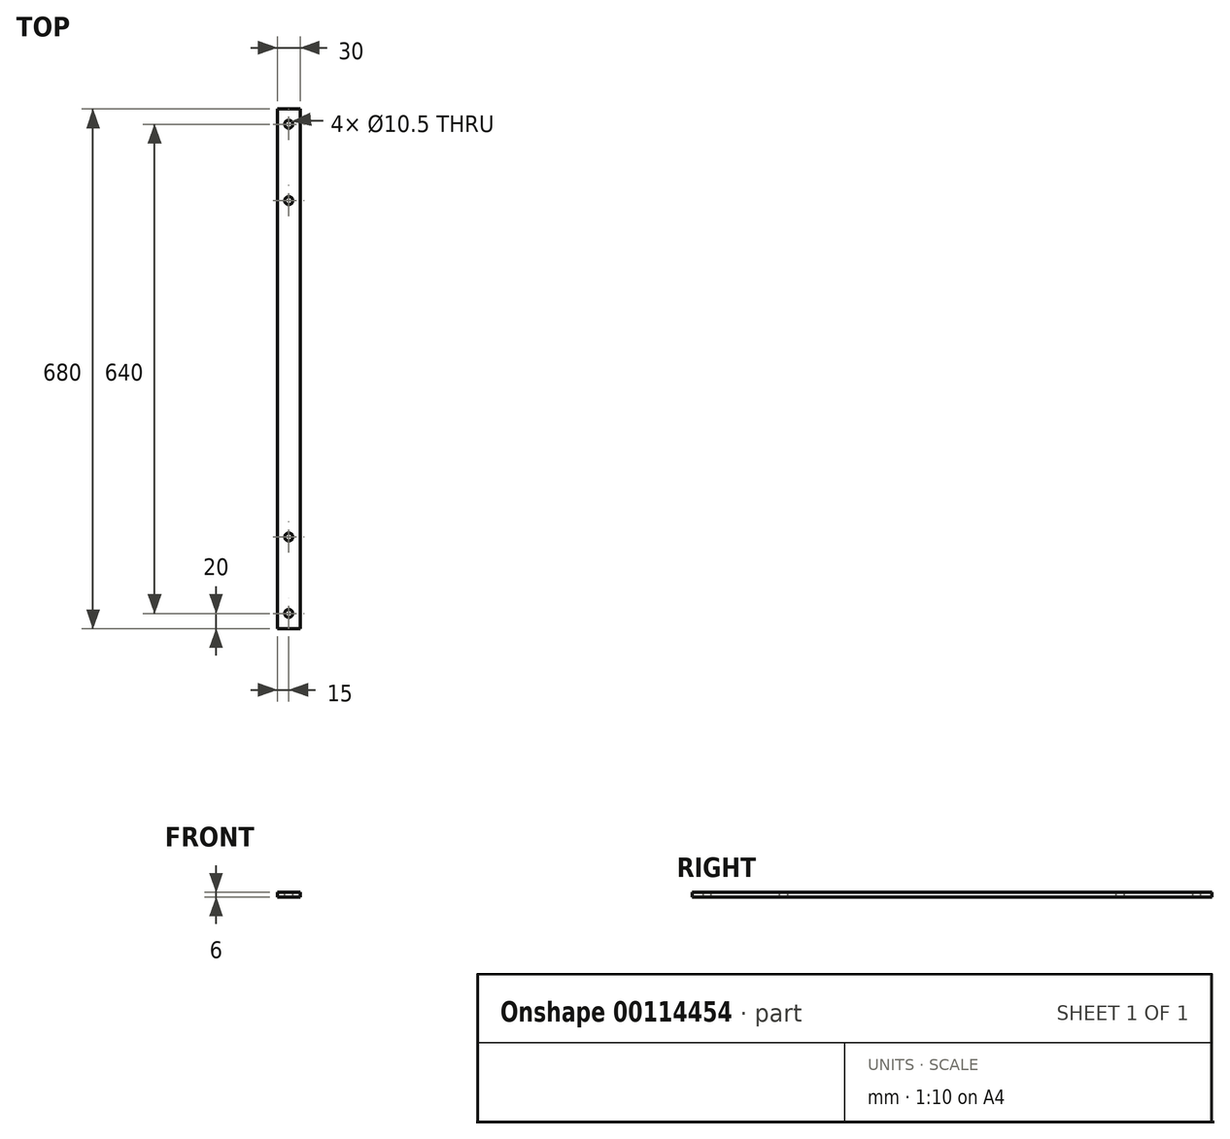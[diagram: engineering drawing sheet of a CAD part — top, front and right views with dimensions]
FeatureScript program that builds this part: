
annotation { "Feature Type Name" : "Feature", "Feature Type Description" : "" }
export const myFeature = defineFeature(function(context is Context, id is Id, definition is map)
    precondition{}
    {
        {
            var Q0;
            Q0=qCreatedBy(makeId("Top.planeOp"),FACE);
            var sketch = newSketch(context, id + "F0", { "sketchPlane" : qUnion([Q0])});
            skLineSegment(sketch, "E0.bottom", {"start": v(15, -340) * mm, "end": v(-15, -340) * mm});
            skLineSegment(sketch, "E0.top", {"start": v(15, 340) * mm, "end": v(-15, 340) * mm});
            skLineSegment(sketch, "E0.left", {"start": v(15, -340) * mm, "end": v(15, 340) * mm});
            skLineSegment(sketch, "E0.right", {"start": v(-15, -340) * mm, "end": v(-15, 340) * mm});
            skPoint(sketch, "E0.middle", {"position": v(0, 0) * mm});
            skSolve(sketch);
        }
        {
            var Q0;
            Q0=makeQuery(id+"F0.imprint","IMPRINT",FACE,{"disambiguationData":[TD([[makeQuery(id+"F0.imprint","IMPRINT",EDGE,{"derivedFrom":sQuery(id+"F0.wireOp",EDGE,"E0.bottom")}),-1.0]])]});
            extrude(context, id + "F1", {"entities" : qUnion([Q0]), "depth" : 6 * mm});
        }
        {
            var Q0;
            Q0=makeQuery(id+"F1.opExtrude","CAP_FACE",FACE,{"disambiguationData":[OSD([sQuery(id+"F0.wireOp",EDGE,"E0.bottom"),sQuery(id+"F0.wireOp",EDGE,"E0.top"),sQuery(id+"F0.wireOp",EDGE,"E0.left"),sQuery(id+"F0.wireOp",EDGE,"E0.right")])],"isStart":false});
            var sketch = newSketch(context, id + "F2", { "sketchPlane" : qUnion([Q0])});
            skCircle(sketch, "E1", {"center": v(0, 320) * mm, "radius": 5.25 * mm});
            skPoint(sketch, "E1.centerSnap0", {"position": v(0, 340) * mm});
            skCircle(sketch, "E2", {"center": v(0, 220) * mm, "radius": 5.25 * mm});
            skCircle(sketch, "E3.MirrorC", {"center": v(0, -220) * mm, "radius": 5.25 * mm});
            skCircle(sketch, "E4.MirrorC", {"center": v(0, -320) * mm, "radius": 5.25 * mm});
            skSolve(sketch);
        }
        {
            var Q0;
            Q0 = qSketchRegion(id + "F2", true);
            extrude(context, id + "F3", {"entities" : qUnion([Q0]), "operationType" : NewBodyOperationType.REMOVE, "oppositeDirection" : true, "depth" : 25 * mm});
        }
    });
